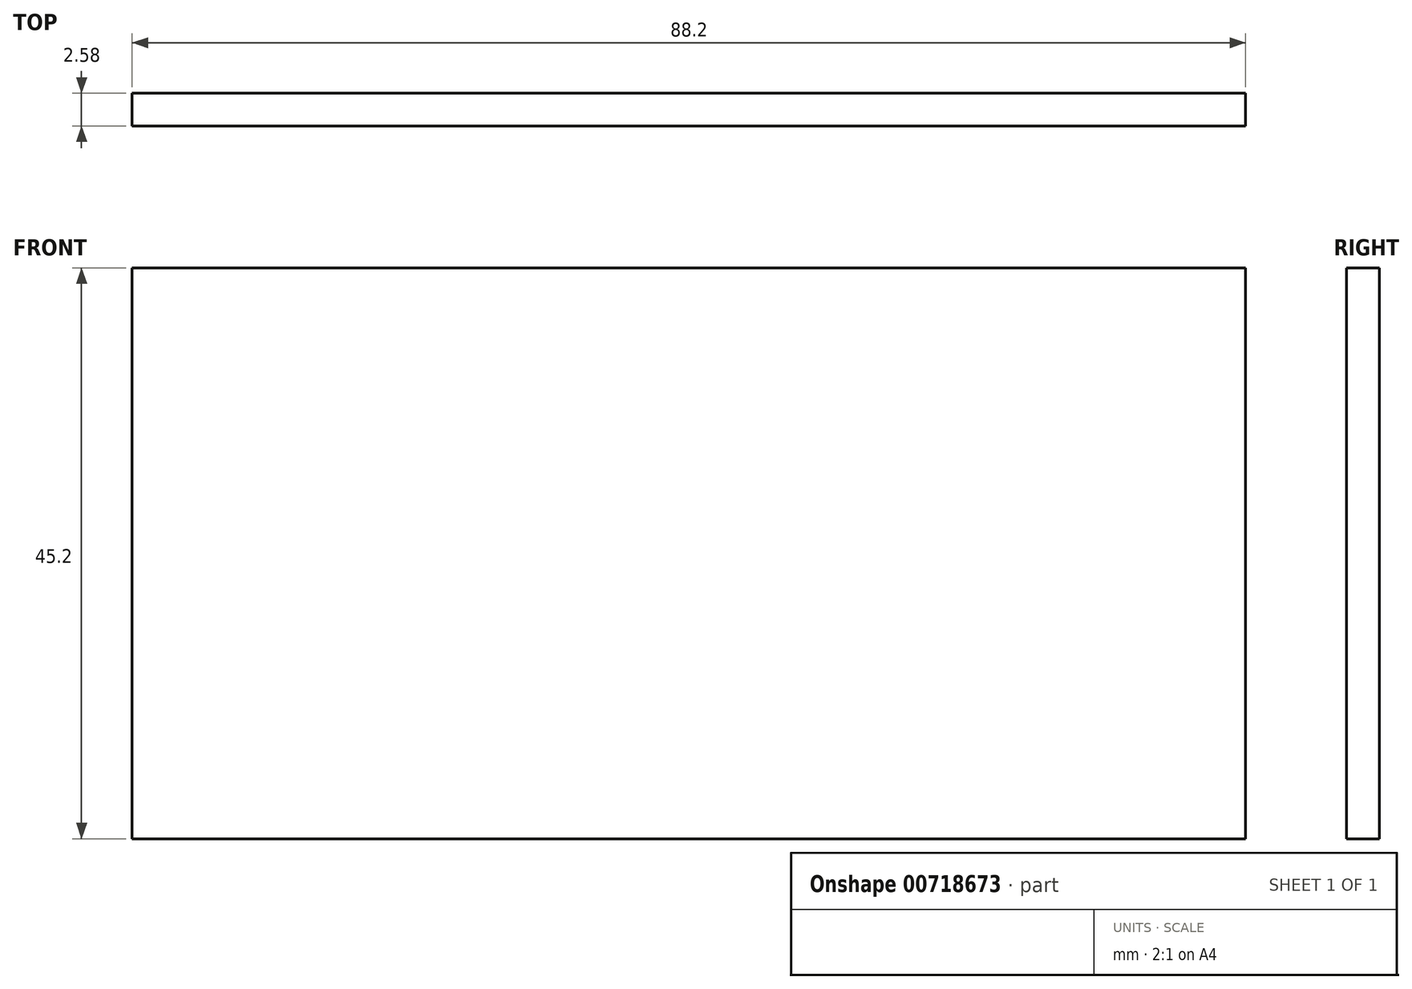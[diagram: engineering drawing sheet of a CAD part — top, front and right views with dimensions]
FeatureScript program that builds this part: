
annotation { "Feature Type Name" : "Feature", "Feature Type Description" : "" }
export const myFeature = defineFeature(function(context is Context, id is Id, definition is map)
    precondition{}
    {
        {
            var Q0;
            Q0=qCreatedBy(makeId("Front.planeOp"),FACE);
            var sketch = newSketch(context, id + "F0", { "sketchPlane" : qUnion([Q0])});
            skLineSegment(sketch, "E0.bottom", {"start": v(-52.59, 59.95) * mm, "end": v(35.6, 59.95) * mm});
            skLineSegment(sketch, "E0.top", {"start": v(-52.59, 14.75) * mm, "end": v(35.6, 14.75) * mm});
            skLineSegment(sketch, "E0.left", {"start": v(-52.59, 59.95) * mm, "end": v(-52.59, 14.75) * mm});
            skLineSegment(sketch, "E0.right", {"start": v(35.6, 59.95) * mm, "end": v(35.6, 14.75) * mm});
            skSolve(sketch);
        }
        {
            var Q0;
            Q0=makeQuery(id+"F0.imprint","IMPRINT",FACE,{"disambiguationData":[TD([[makeQuery(id+"F0.imprint","IMPRINT",EDGE,{"derivedFrom":sQuery(id+"F0.wireOp",EDGE,"E0.bottom")}),-1.0]])]});
            var sketch = newSketch(context, id + "F1", { "sketchPlane" : qUnion([Q0])});
            skLineSegment(sketch, "E1", {"start": v(-109.54, 55.15) * mm, "end": v(-111.17, 12.9) * mm});
            skSolve(sketch);
        }
        {
            var Q0;
            Q0=makeQuery(id+"F1.imprint","IMPRINT",FACE,{"disambiguationData":[TD([[makeQuery(id+"F1.imprint","IMPRINT",EDGE,{"derivedFrom":makeQuery(id+"F0.imprint","IMPRINT",EDGE,{"derivedFrom":sQuery(id+"F0.wireOp",EDGE,"E0.bottom")})}),-1.0]])]});
            extrude(context, id + "F2", {"entities" : qUnion([Q0]), "endBound" : BoundingType.SYMMETRIC, "depth" : 2.58 * mm, "offsetDistance" : 25.4 * mm});
        }
    });
